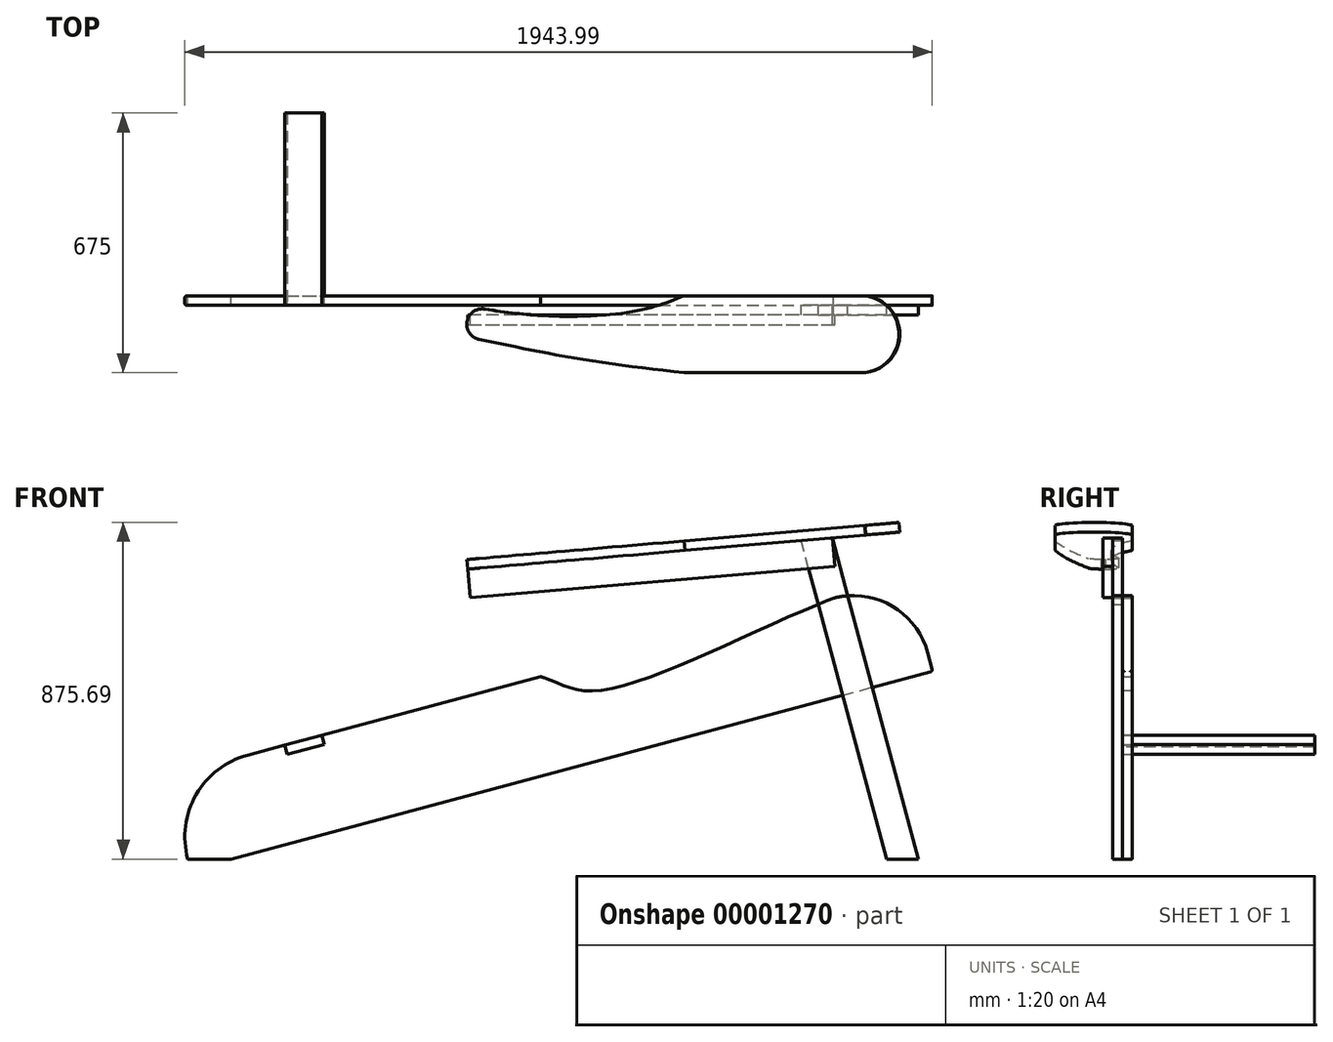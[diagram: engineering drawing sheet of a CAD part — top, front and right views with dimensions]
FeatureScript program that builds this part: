
annotation { "Feature Type Name" : "Feature", "Feature Type Description" : "" }
export const myFeature = defineFeature(function(context is Context, id is Id, definition is map)
    precondition{}
    {
        {
            var Q0;
            Q0=qCreatedBy(makeId("Front.planeOp"),FACE);
            var sketch = newSketch(context, id + "F0", { "sketchPlane" : qUnion([Q0])});
            skLineSegment(sketch, "E0", {"start": v(83.2, 22.3) * mm, "end": v(1908.22, 511.3) * mm});
            skLineSegment(sketch, "E1", {"start": v(1908.22, 511.3) * mm, "end": v(1895.3, 559.55) * mm});
            skLineSegment(sketch, "E2", {"start": v(888.26, 496.77) * mm, "end": v(319.36, 344.33) * mm});
            skPoint(sketch, "E3.visualSharp", {"position": v(-69.83, 240.05) * mm});
            skArc(sketch, "E3.filletArc", {"start": v(126.17, 292.57) * mm, "mid": v(-7.63, 189.7) * mm, "end": v(-29.16, 22.3) * mm});
            skPoint(sketch, "E4.visualSharp", {"position": v(1843.53, 752.73) * mm});
            skArc(sketch, "E4.filletArc", {"start": v(1895.3, 559.55) * mm, "mid": v(1802.11, 681) * mm, "end": v(1650.35, 700.97) * mm});
            skFitSpline(sketch, "E5", {"points": [v(888.26, 496.77) * mm, v(1031.49, 460) * mm, v(1650.35, 700.97) * mm], "startDerivative": vector(449.08, -126.77) * mm, "endDerivative": vector(910.14, 354.4) * mm});
            skLineSegment(sketch, "E6", {"start": v(222.77, 318.45) * mm, "end": v(229.24, 294.3) * mm});
            skLineSegment(sketch, "E7", {"start": v(229.24, 294.3) * mm, "end": v(325.83, 320.18) * mm});
            skLineSegment(sketch, "E8", {"start": v(325.83, 320.18) * mm, "end": v(319.36, 344.33) * mm});
            skLineSegment(sketch, "E9.trimOffspring", {"start": v(222.77, 318.45) * mm, "end": v(126.17, 292.57) * mm});
            skLineSegment(sketch, "E10", {"start": v(-29.16, 22.3) * mm, "end": v(2295.57, 22.3) * mm, "construction": true});
            skLineSegment(sketch, "E11", {"start": v(-29.16, 22.3) * mm, "end": v(83.2, 22.3) * mm});
            skPoint(sketch, "E12.orphan", {"position": v(0, 0) * mm});
            skLineSegment(sketch, "E13", {"start": v(888.26, 496.77) * mm, "end": v(853.4, 626.85) * mm, "construction": true});
            skLineSegment(sketch, "E14", {"start": v(853.4, 626.85) * mm, "end": v(800.11, 612.57) * mm});
            skLineSegment(sketch, "E15", {"start": v(793.04, 600.33) * mm, "end": v(825.31, 479.9) * mm, "construction": true});
            skPoint(sketch, "E16.visualSharp", {"position": v(790.45, 609.99) * mm});
            skPoint(sketch, "E17.visualSharp", {"position": v(853.4, 626.85) * mm});
            skLineSegment(sketch, "E18", {"start": v(810.47, 573.94) * mm, "end": v(854.1, 585.63) * mm});
            skLineSegment(sketch, "E19", {"start": v(861.17, 597.88) * mm, "end": v(853.4, 626.85) * mm});
            skPoint(sketch, "E20.visualSharp", {"position": v(800.8, 571.35) * mm});
            skPoint(sketch, "E21.visualSharp", {"position": v(863.76, 588.22) * mm});
            skArc(sketch, "E21.filletArc", {"start": v(854.1, 585.63) * mm, "mid": v(860.17, 590.29) * mm, "end": v(861.17, 597.88) * mm});
            skArc(sketch, "E22", {"start": v(800.11, 612.57) * mm, "mid": v(785.97, 588.08) * mm, "end": v(810.47, 573.94) * mm});
            skSolve(sketch);
        }
        {
            var Q0;
            {var subQ1=sQuery(id+"F0.wireOp",EDGE,"E2");Q0=makeQuery(id+"F0.imprint","IMPRINT",FACE,{"disambiguationData":[TD([[makeQuery(id+"F0.imprint","IMPRINT",EDGE,{"derivedFrom":subQ1}),1.0]])]});}
            var sketch = newSketch(context, id + "F1", { "sketchPlane" : qUnion([Q0])});
            skLineSegment(sketch, "E23", {"start": v(-29.16, 22.3) * mm, "end": v(2290.4, 22.3) * mm, "construction": true});
            skLineSegment(sketch, "E24", {"start": v(1788.37, 22.3) * mm, "end": v(1531.3, 981.72) * mm});
            skLineSegment(sketch, "E25", {"start": v(1531.3, 981.72) * mm, "end": v(1608.57, 1002.42) * mm});
            skLineSegment(sketch, "E26", {"start": v(1608.57, 1002.42) * mm, "end": v(1871.2, 22.3) * mm});
            skLineSegment(sketch, "E27", {"start": v(1871.2, 22.3) * mm, "end": v(1788.37, 22.3) * mm});
            skSolve(sketch);
        }
        {
            var Q0;
            Q0=makeQuery(id+"F0.imprint","IMPRINT",FACE,{"disambiguationData":[TD([[makeQuery(id+"F0.imprint","IMPRINT",EDGE,{"derivedFrom":sQuery(id+"F0.wireOp",EDGE,"E0")}),1.0]])]});
            extrude(context, id + "F2", {"entities" : qUnion([Q0]), "depth" : 25 * mm});
        }
        {
            var Q0;
            Q0=makeQuery(id+"F2.opExtrude","CAP_EDGE",EDGE,{"disambiguationData":[OSD([sQuery(id+"F0.wireOp",EDGE,"E2")])],"isStart":false});
            var Q1;
            Q1=makeQuery(id+"F2.opExtrude","CAP_EDGE",EDGE,{"disambiguationData":[OSD([sQuery(id+"F0.wireOp",EDGE,"E2")])],"isStart":true});
            var Q2;
            Q2=makeQuery(id+"F2.opExtrude","CAP_EDGE",EDGE,{"disambiguationData":[OSD([sQuery(id+"F0.wireOp",EDGE,"E0")])],"isStart":false});
            var Q3;
            Q3=makeQuery(id+"F2.opExtrude","SWEPT_EDGE",EDGE,{"disambiguationData":[OSD([sQuery(id+"F0.wireOp",EDGE,"E0"),sQuery(id+"F0.wireOp",EDGE,"E1")])]});
            var Q4;
            Q4=makeQuery(id+"F2.opExtrude","CAP_EDGE",EDGE,{"disambiguationData":[OSD([sQuery(id+"F0.wireOp",EDGE,"E0")])],"isStart":true});
            var Q5;
            Q5=makeQuery(id+"F2.opExtrude","CAP_EDGE",EDGE,{"disambiguationData":[OSD([sQuery(id+"F0.wireOp",EDGE,"E9.trimOffspring")])],"isStart":true});
            var Q6;
            Q6=makeQuery(id+"F2.opExtrude","CAP_EDGE",EDGE,{"disambiguationData":[OSD([sQuery(id+"F0.wireOp",EDGE,"E9.trimOffspring")])],"isStart":false});
            fillet(context, id + "F3", {"entities" : qUnion([Q0, Q1, Q2, Q3, Q4, Q5, Q6]), "radius" : 5 * mm, "tangentPropagation" : true, "allowEdgeOverflow" : false});
        }
        {
            var Q0;
            {var subQ5=sQuery(id+"F1.wireOp",EDGE,"E25");Q0=makeQuery(id+"F1.imprint","IMPRINT",FACE,{"disambiguationData":[TD([[makeQuery(id+"F1.imprint","IMPRINT",EDGE,{"derivedFrom":subQ5}),-1.0]])]});}
            var sketch = newSketch(context, id + "F4", { "sketchPlane" : qUnion([Q0])});
            skPoint(sketch, "E28", {"position": v(1547.28, 849.42) * mm});
            skLineSegment(sketch, "E29", {"start": v(1547.28, 849.42) * mm, "end": v(699, 776.63) * mm});
            skLineSegment(sketch, "E30", {"start": v(699, 776.63) * mm, "end": v(696.86, 801.54) * mm});
            skLineSegment(sketch, "E31", {"start": v(696.86, 801.54) * mm, "end": v(1827.1, 898.52) * mm});
            skLineSegment(sketch, "E32", {"start": v(1827.1, 898.52) * mm, "end": v(1829.25, 873.6) * mm});
            skLineSegment(sketch, "E33", {"start": v(1829.25, 873.6) * mm, "end": v(1547.28, 849.42) * mm});
            skSolve(sketch);
        }
        {
            var Q0;
            {var subQ0=makeQuery(id+"F0.imprint","IMPRINT",EDGE,{"derivedFrom":sQuery(id+"F0.wireOp",EDGE,"E5")});var subQ1=makeQuery(id+"F0.imprint","IMPRINT",EDGE,{"derivedFrom":sQuery(id+"F0.wireOp",EDGE,"E4.filletArc")});var subQ2=makeQuery(id+"F1.imprint","INTERSECT",VERTEX,{"derivedFrom":[subQ1,subQ0]});var subQ12=makeQuery(id+"F1.imprint","IMPRINT",EDGE,{"disambiguationData":[TD([[subQ2,1.0]])],"derivedFrom":subQ1});Q0=makeQuery(id+"F4.imprint","IMPRINT",FACE,{"disambiguationData":[TD([[makeQuery(id+"F4.imprint","IMPRINT",EDGE,{"derivedFrom":subQ12}),-1.0]])]});}
            var Q1;
            {var subQ5=sQuery(id+"F1.wireOp",EDGE,"E24");var subQ6=makeQuery(id+"F0.imprint","IMPRINT",EDGE,{"derivedFrom":sQuery(id+"F0.wireOp",EDGE,"E0")});var subQ7=makeQuery(id+"F1.imprint","INTERSECT",VERTEX,{"derivedFrom":[subQ6,subQ5]});Q1=makeQuery(id+"F1.imprint","IMPRINT",FACE,{"disambiguationData":[TD([[makeQuery(id+"F1.imprint","IMPRINT",EDGE,{"disambiguationData":[TD([[subQ7,-1.0]])],"derivedFrom":subQ5}),-1.0]])]});}
            var Q2;
            {var subQ0=sQuery(id+"F1.wireOp",EDGE,"E27");Q2=makeQuery(id+"F1.imprint","IMPRINT",FACE,{"disambiguationData":[TD([[makeQuery(id+"F1.imprint","IMPRINT",EDGE,{"derivedFrom":subQ0}),-1.0]])]});}
            extrude(context, id + "F5", {"entities" : qUnion([Q0, Q1, Q2]), "depth" : 50 * mm, "hasSecondDirection" : true, "secondDirectionOppositeDirection" : false, "secondDirectionDepth" : 25 * mm});
        }
        {
            var Q0;
            {var subQ1=sQuery(id+"F4.wireOp",EDGE,"E29");Q0=makeQuery(id+"F4.imprint","IMPRINT",FACE,{"disambiguationData":[TD([[makeQuery(id+"F4.imprint","IMPRINT",EDGE,{"derivedFrom":subQ1}),-1.0]])]});}
            var Q1;
            {var subQ0=sQuery(id+"F4.wireOp",EDGE,"E31");var subQ1=sQuery(id+"F1.wireOp",EDGE,"E25");var subQ2=sQuery(id+"F1.wireOp",EDGE,"E24");var subQ3=makeQuery(id+"F1.imprint","IMPRINT",EDGE,{"disambiguationData":[TD([[makeQuery(id+"F1.imprint","INTERSECT",VERTEX,{"derivedFrom":[subQ2,subQ1]}),1.0]])],"derivedFrom":subQ2});var subQ4=makeQuery(id+"F4.imprint","INTERSECT",VERTEX,{"derivedFrom":[subQ3,subQ0]});Q1=makeQuery(id+"F4.imprint","IMPRINT",FACE,{"disambiguationData":[TD([[makeQuery(id+"F4.imprint","IMPRINT",EDGE,{"disambiguationData":[TD([[subQ4,-1.0]])],"derivedFrom":subQ0}),-1.0]])]});}
            var Q2;
            {var subQ0=sQuery(id+"F4.wireOp",EDGE,"E32");Q2=makeQuery(id+"F4.imprint","IMPRINT",FACE,{"disambiguationData":[TD([[makeQuery(id+"F4.imprint","IMPRINT",EDGE,{"derivedFrom":subQ0}),-1.0]])]});}
            extrude(context, id + "F6", {"entities" : qUnion([Q0, Q1, Q2]), "operationType" : NewBodyOperationType.ADD, "depth" : 200 * mm});
        }
        {
            var Q0;
            Q0=makeQuery(id+"F6.opExtrude","SWEPT_FACE",FACE,{"disambiguationData":[OSD([sQuery(id+"F4.wireOp",EDGE,"E29"),sQuery(id+"F4.wireOp",EDGE,"E33")])]});
            var sketch = newSketch(context, id + "F7", { "sketchPlane" : qUnion([Q0])});
            skLineSegment(sketch, "E34", {"start": v(1714.59, 50) * mm, "end": v(762.83, 50) * mm});
            skLineSegment(sketch, "E35", {"start": v(762.83, 50) * mm, "end": v(762.83, 75) * mm});
            skLineSegment(sketch, "E36", {"start": v(762.83, 75) * mm, "end": v(1714.59, 75) * mm});
            skLineSegment(sketch, "E37", {"start": v(1714.59, 75) * mm, "end": v(1714.59, 50) * mm});
            skSolve(sketch);
        }
        {
            var Q0;
            {var subQ0=sQuery(id+"F7.wireOp",EDGE,"E35");Q0=makeQuery(id+"F7.imprint","IMPRINT",FACE,{"disambiguationData":[TD([[makeQuery(id+"F7.imprint","IMPRINT",EDGE,{"derivedFrom":subQ0}),1.0]])]});}
            extrude(context, id + "F8", {"entities" : qUnion([Q0]), "depth" : 75 * mm});
        }
        {
            var Q0;
            Q0=makeQuery(id+"F6.opExtrude","SWEPT_FACE",FACE,{"disambiguationData":[OSD([sQuery(id+"F4.wireOp",EDGE,"E31")])]});
            var sketch = newSketch(context, id + "F9", { "sketchPlane" : qUnion([Q0])});
            skArc(sketch, "E38", {"start": v(1778.62, -200) * mm, "mid": v(1890.89, -101.76) * mm, "end": v(1781.8, 0) * mm});
            skLineSegment(sketch, "E39", {"start": v(762.83, 0) * mm, "end": v(1781.8, 0) * mm});
            skLineSegment(sketch, "E40", {"start": v(1778.62, -200) * mm, "end": v(762.83, -200) * mm});
            skLineSegment(sketch, "E41", {"start": v(762.83, -200) * mm, "end": v(762.83, 0) * mm});
            skFitSpline(sketch, "E42", {"points": [v(1330.03, -200) * mm, v(999.8, -154.58) * mm, v(794.7, -113.5) * mm], "startDerivative": vector(-629.24, 66.05) * mm, "endDerivative": vector(-432.44, 84.8) * mm});
            skFitSpline(sketch, "E43", {"points": [v(1330.03, 0) * mm, v(1196.3, -41.2) * mm, v(809.18, -34.82) * mm], "startDerivative": vector(-307.14, -128.03) * mm, "endDerivative": vector(-697.7, 119.96) * mm});
            skArc(sketch, "E44", {"start": v(809.18, -34.82) * mm, "mid": v(763.06, -67) * mm, "end": v(794.7, -113.5) * mm});
            skSolve(sketch);
        }
        {
            var Q0;
            {var subQ3=sQuery(id+"F9.wireOp",EDGE,"E42");Q0=makeQuery(id+"F9.imprint","IMPRINT",FACE,{"disambiguationData":[TD([[makeQuery(id+"F9.imprint","IMPRINT",EDGE,{"derivedFrom":subQ3}),1.0]])]});}
            var Q1;
            {var subQ3=sQuery(id+"F9.wireOp",EDGE,"E43");Q1=makeQuery(id+"F9.imprint","IMPRINT",FACE,{"disambiguationData":[TD([[makeQuery(id+"F9.imprint","IMPRINT",EDGE,{"derivedFrom":subQ3}),-1.0]])]});}
            var Q2;
            {var subQ1=sQuery(id+"F4.wireOp",EDGE,"E31");var subQ6=makeQuery(id+"F6.opExtrude","SWEPT_EDGE",EDGE,{"disambiguationData":[OSD([subQ1,sQuery(id+"F4.wireOp",EDGE,"E32")])]});Q2=makeQuery(id+"F9.imprint","IMPRINT",FACE,{"disambiguationData":[TD([[makeQuery(id+"F9.imprint","IMPRINT",EDGE,{"derivedFrom":subQ6}),1.0]])]});}
            var Q3;
            Q3=makeQuery(id+"F6.opExtrude","SWEPT_FACE",FACE,{"disambiguationData":[OSD([sQuery(id+"F4.wireOp",EDGE,"E29"),sQuery(id+"F4.wireOp",EDGE,"E33")])]});
            extrude(context, id + "F10", {"entities" : qUnion([Q0, Q1, Q2]), "operationType" : NewBodyOperationType.REMOVE, "endBound" : BoundingType.UP_TO_SURFACE, "oppositeDirection" : true, "endBoundEntityFace" : qUnion([Q3]), "depth" : 25 * mm});
        }
        {
            var Q0;
            Q0=makeQuery(id+"F2.opExtrude","CAP_FACE",FACE,{"disambiguationData":[OSD([sQuery(id+"F0.wireOp",EDGE,"E0"),sQuery(id+"F0.wireOp",EDGE,"E1"),sQuery(id+"F0.wireOp",EDGE,"E2"),sQuery(id+"F0.wireOp",EDGE,"E3.filletArc"),sQuery(id+"F0.wireOp",EDGE,"E4.filletArc"),sQuery(id+"F0.wireOp",EDGE,"E5"),sQuery(id+"F0.wireOp",EDGE,"E6"),sQuery(id+"F0.wireOp",EDGE,"E7"),sQuery(id+"F0.wireOp",EDGE,"E8"),sQuery(id+"F0.wireOp",EDGE,"E9.trimOffspring"),sQuery(id+"F0.wireOp",EDGE,"E11")])],"isStart":false});
            var sketch = newSketch(context, id + "F11", { "sketchPlane" : qUnion([Q0])});
            skLineSegment(sketch, "E45", {"start": v(229.24, 294.3) * mm, "end": v(325.83, 320.18) * mm});
            skLineSegment(sketch, "E46", {"start": v(325.83, 320.18) * mm, "end": v(319.36, 344.33) * mm});
            skLineSegment(sketch, "E47", {"start": v(319.36, 344.33) * mm, "end": v(222.5, 318.38) * mm});
            skLineSegment(sketch, "E48", {"start": v(222.5, 318.38) * mm, "end": v(229.24, 294.3) * mm});
            skSolve(sketch);
        }
        {
            var Q0;
            {var subQ2=sQuery(id+"F11.wireOp",EDGE,"E45");Q0=makeQuery(id+"F11.imprint","IMPRINT",FACE,{"disambiguationData":[TD([[makeQuery(id+"F11.imprint","IMPRINT",EDGE,{"derivedFrom":subQ2}),1.0]])]});}
            extrude(context, id + "F12", {"entities" : qUnion([Q0]), "oppositeDirection" : true, "depth" : 500 * mm});
        }
    });
